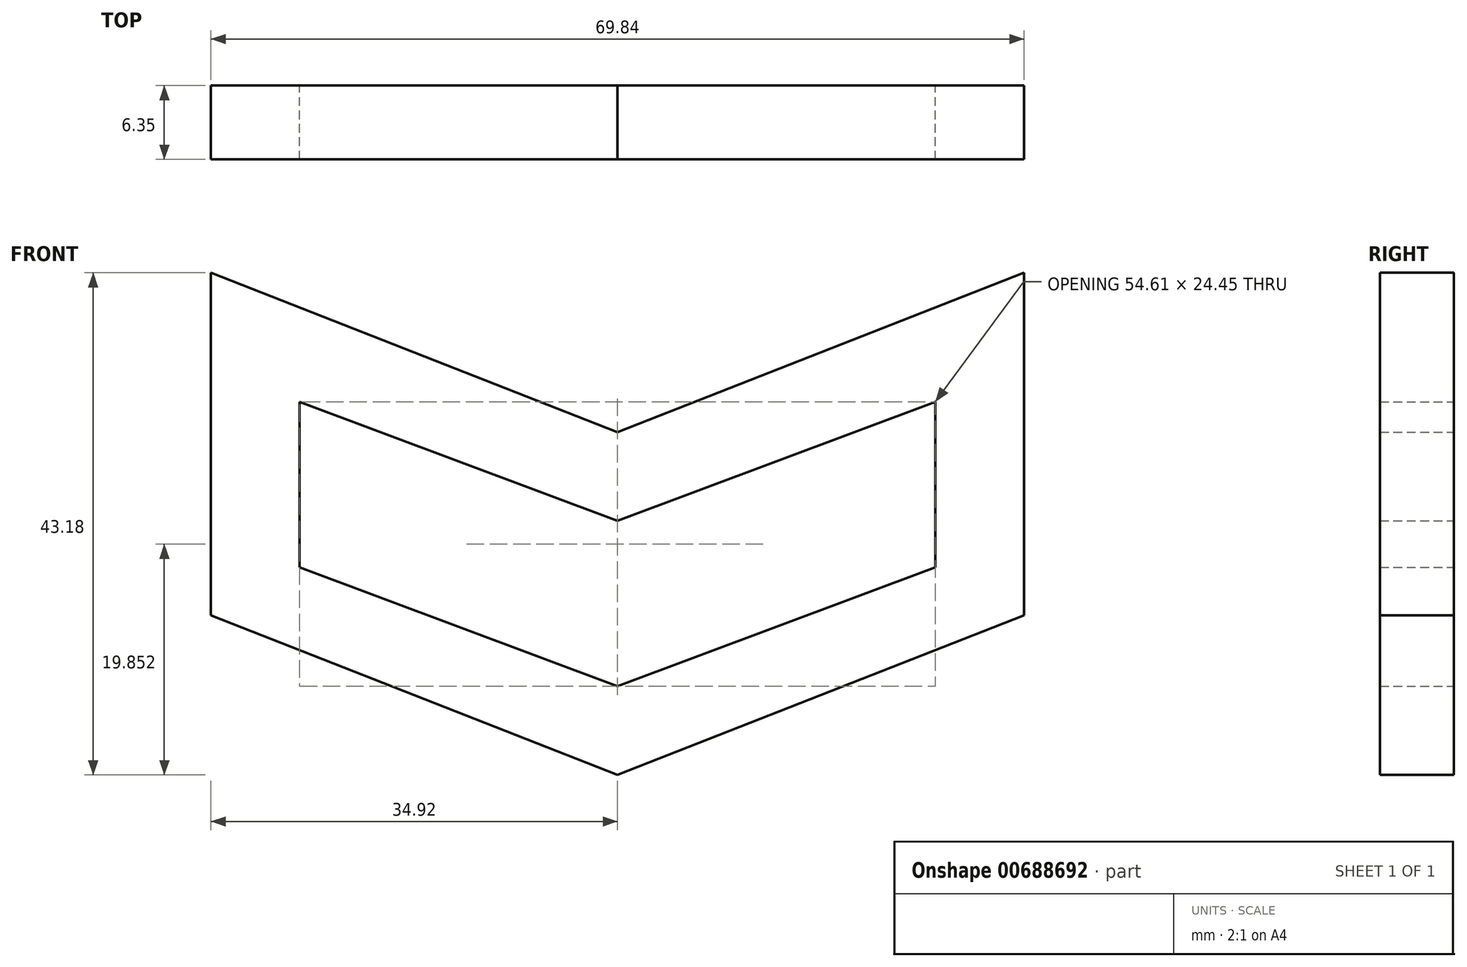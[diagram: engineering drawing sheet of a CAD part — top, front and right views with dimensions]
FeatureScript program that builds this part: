
annotation { "Feature Type Name" : "Feature", "Feature Type Description" : "" }
export const myFeature = defineFeature(function(context is Context, id is Id, definition is map)
    precondition{}
    {
        {
            var Q0;
            Q0=qCreatedBy(makeId("Front.planeOp"),FACE);
            var sketch = newSketch(context, id + "F0", { "sketchPlane" : qUnion([Q0])});
            skLineSegment(sketch, "E0", {"start": v(0, 4.93) * mm, "end": v(0, -24.53) * mm});
            skLineSegment(sketch, "E1", {"start": v(0, -24.53) * mm, "end": v(-34.92, -10.8) * mm});
            skLineSegment(sketch, "E2", {"start": v(0, 4.93) * mm, "end": v(-34.93, 18.65) * mm});
            skLineSegment(sketch, "E3", {"start": v(-34.93, 18.65) * mm, "end": v(-34.92, -10.8) * mm});
            skLineSegment(sketch, "E4", {"start": v(0, -2.69) * mm, "end": v(-27.3, 7.55) * mm});
            skLineSegment(sketch, "E5", {"start": v(-27.3, 7.55) * mm, "end": v(-27.3, -6.67) * mm});
            skLineSegment(sketch, "E6", {"start": v(-27.3, -6.67) * mm, "end": v(0, -16.9) * mm});
            skLineSegment(sketch, "E7.MirrorCS", {"start": v(0, 4.93) * mm, "end": v(34.93, 18.65) * mm});
            skLineSegment(sketch, "E8.MirrorCS", {"start": v(34.93, 18.65) * mm, "end": v(34.93, -10.8) * mm});
            skLineSegment(sketch, "E9.MirrorCS", {"start": v(0, -24.53) * mm, "end": v(34.92, -10.8) * mm});
            skLineSegment(sketch, "E10.MirrorCS", {"start": v(27.3, -6.67) * mm, "end": v(0, -16.9) * mm});
            skLineSegment(sketch, "E11.MirrorCS", {"start": v(27.3, 7.55) * mm, "end": v(27.3, -6.67) * mm});
            skLineSegment(sketch, "E12.MirrorCS", {"start": v(0, -2.69) * mm, "end": v(27.3, 7.55) * mm});
            skLineSegment(sketch, "E13", {"start": v(0, 4.93) * mm, "end": v(0, 0) * mm});
            skLineSegment(sketch, "E14", {"start": v(0, -24.53) * mm, "end": v(0, -16.9) * mm});
            skSolve(sketch);
        }
        {
            var Q0;
            Q0 = qSketchRegion(id + "F0", true);
            extrude(context, id + "F1", {"entities" : qUnion([Q0]), "depth" : 6.35 * mm, "offsetDistance" : 25.4 * mm});
        }
    });
